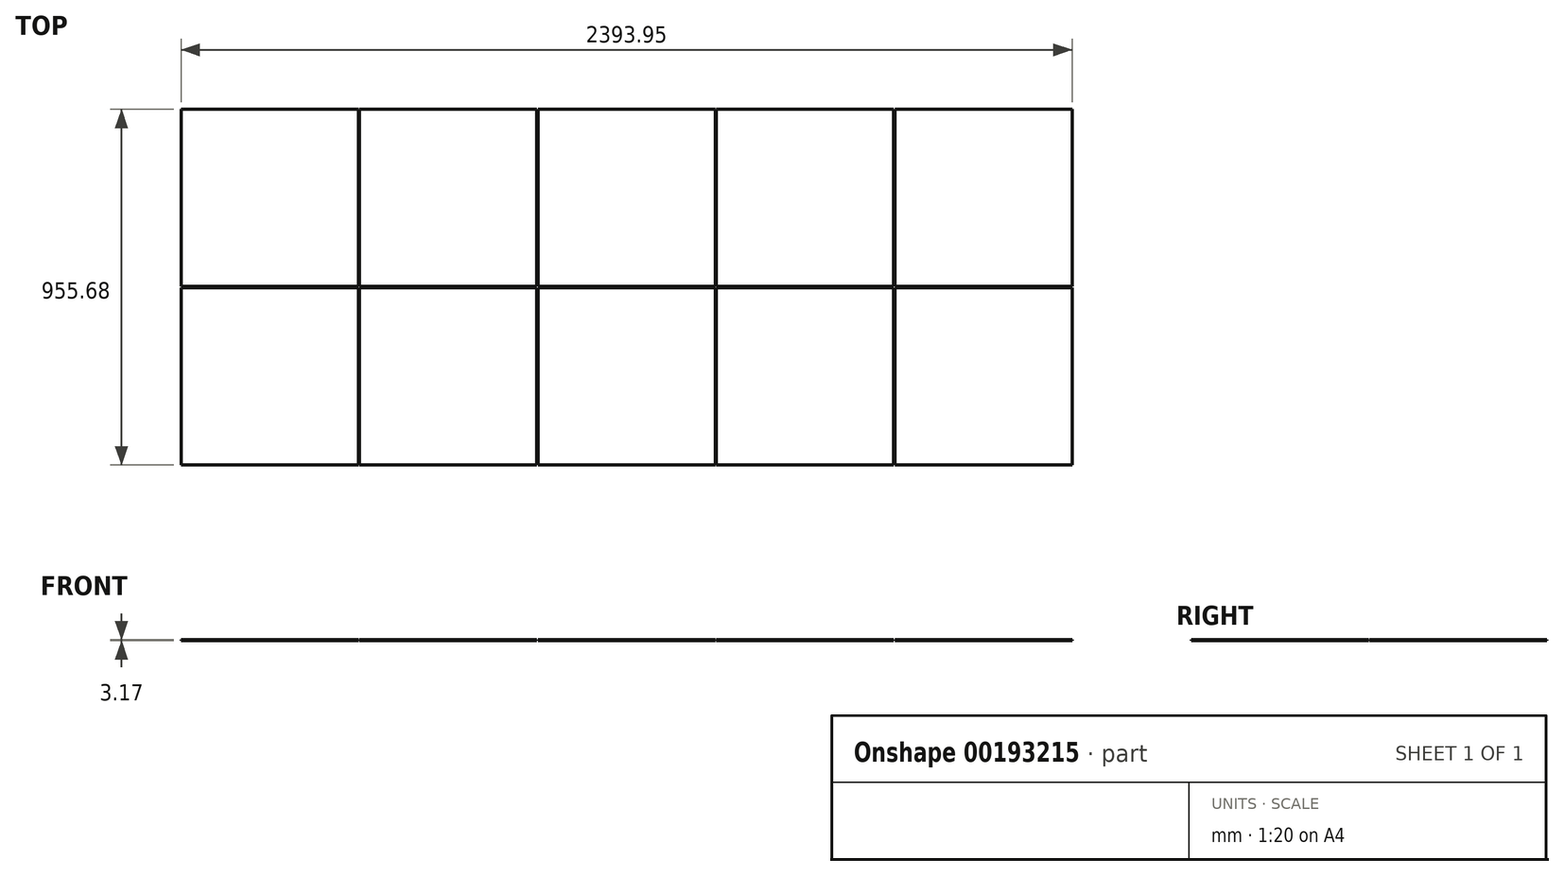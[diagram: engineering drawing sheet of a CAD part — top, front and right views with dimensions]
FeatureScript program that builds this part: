
annotation { "Feature Type Name" : "Feature", "Feature Type Description" : "" }
export const myFeature = defineFeature(function(context is Context, id is Id, definition is map)
    precondition{}
    {
        {
            var Q0;
            Q0=qCreatedBy(makeId("Top.planeOp"),FACE);
            var sketch = newSketch(context, id + "F0", { "sketchPlane" : qUnion([Q0])});
            skLineSegment(sketch, "E0.bottom", {"start": v(0, 0) * mm, "end": v(476.25, 0) * mm});
            skLineSegment(sketch, "E0.top", {"start": v(0, -476.25) * mm, "end": v(476.25, -476.25) * mm});
            skLineSegment(sketch, "E0.left", {"start": v(0, 0) * mm, "end": v(0, -476.25) * mm});
            skLineSegment(sketch, "E0.right", {"start": v(476.25, 0) * mm, "end": v(476.25, -476.25) * mm});
            skLineSegment(sketch, "E1.0.1.0", {"start": v(476.25, 479.43) * mm, "end": v(476.25, 3.18) * mm});
            skLineSegment(sketch, "E1.0.1.1", {"start": v(0, 3.18) * mm, "end": v(476.25, 3.18) * mm});
            skLineSegment(sketch, "E1.0.1.2", {"start": v(0, 479.43) * mm, "end": v(0, 3.18) * mm});
            skLineSegment(sketch, "E1.0.1.3", {"start": v(0, 479.43) * mm, "end": v(476.25, 479.43) * mm});
            skLineSegment(sketch, "E1.1.0.0", {"start": v(955.68, 0) * mm, "end": v(955.68, -476.25) * mm});
            skLineSegment(sketch, "E1.1.0.1", {"start": v(479.43, -476.25) * mm, "end": v(955.68, -476.25) * mm});
            skLineSegment(sketch, "E1.1.0.2", {"start": v(479.43, 0) * mm, "end": v(479.43, -476.25) * mm});
            skLineSegment(sketch, "E1.1.0.3", {"start": v(479.43, 0) * mm, "end": v(955.68, 0) * mm});
            skLineSegment(sketch, "E1.1.1.0", {"start": v(955.68, 479.43) * mm, "end": v(955.68, 3.18) * mm});
            skLineSegment(sketch, "E1.1.1.1", {"start": v(479.43, 3.18) * mm, "end": v(955.68, 3.18) * mm});
            skLineSegment(sketch, "E1.1.1.2", {"start": v(479.43, 479.43) * mm, "end": v(479.43, 3.18) * mm});
            skLineSegment(sketch, "E1.1.1.3", {"start": v(479.43, 479.43) * mm, "end": v(955.68, 479.43) * mm});
            skLineSegment(sketch, "E1.2.0.0", {"start": v(1435.1, 0) * mm, "end": v(1435.1, -476.25) * mm});
            skLineSegment(sketch, "E1.2.0.1", {"start": v(958.85, -476.25) * mm, "end": v(1435.1, -476.25) * mm});
            skLineSegment(sketch, "E1.2.0.2", {"start": v(958.85, 0) * mm, "end": v(958.85, -476.25) * mm});
            skLineSegment(sketch, "E1.2.0.3", {"start": v(958.85, 0) * mm, "end": v(1435.1, 0) * mm});
            skLineSegment(sketch, "E1.2.1.0", {"start": v(1435.1, 479.43) * mm, "end": v(1435.1, 3.18) * mm});
            skLineSegment(sketch, "E1.2.1.1", {"start": v(958.85, 3.18) * mm, "end": v(1435.1, 3.18) * mm});
            skLineSegment(sketch, "E1.2.1.2", {"start": v(958.85, 479.43) * mm, "end": v(958.85, 3.18) * mm});
            skLineSegment(sketch, "E1.2.1.3", {"start": v(958.85, 479.43) * mm, "end": v(1435.1, 479.43) * mm});
            skLineSegment(sketch, "E1.3.0.0", {"start": v(1914.53, 0) * mm, "end": v(1914.53, -476.25) * mm});
            skLineSegment(sketch, "E1.3.0.1", {"start": v(1438.28, -476.25) * mm, "end": v(1914.53, -476.25) * mm});
            skLineSegment(sketch, "E1.3.0.2", {"start": v(1438.27, 0) * mm, "end": v(1438.27, -476.25) * mm});
            skLineSegment(sketch, "E1.3.0.3", {"start": v(1438.27, 0) * mm, "end": v(1914.53, 0) * mm});
            skLineSegment(sketch, "E1.3.1.0", {"start": v(1914.53, 479.43) * mm, "end": v(1914.53, 3.18) * mm});
            skLineSegment(sketch, "E1.3.1.1", {"start": v(1438.28, 3.18) * mm, "end": v(1914.53, 3.18) * mm});
            skLineSegment(sketch, "E1.3.1.2", {"start": v(1438.27, 479.43) * mm, "end": v(1438.27, 3.18) * mm});
            skLineSegment(sketch, "E1.3.1.3", {"start": v(1438.27, 479.43) * mm, "end": v(1914.53, 479.43) * mm});
            skLineSegment(sketch, "E1.4.0.0", {"start": v(2393.95, 0) * mm, "end": v(2393.95, -476.25) * mm});
            skLineSegment(sketch, "E1.4.0.1", {"start": v(1917.7, -476.25) * mm, "end": v(2393.95, -476.25) * mm});
            skLineSegment(sketch, "E1.4.0.2", {"start": v(1917.7, 0) * mm, "end": v(1917.7, -476.25) * mm});
            skLineSegment(sketch, "E1.4.0.3", {"start": v(1917.7, 0) * mm, "end": v(2393.95, 0) * mm});
            skLineSegment(sketch, "E1.4.1.0", {"start": v(2393.95, 479.43) * mm, "end": v(2393.95, 3.18) * mm});
            skLineSegment(sketch, "E1.4.1.1", {"start": v(1917.7, 3.18) * mm, "end": v(2393.95, 3.18) * mm});
            skLineSegment(sketch, "E1.4.1.2", {"start": v(1917.7, 479.43) * mm, "end": v(1917.7, 3.18) * mm});
            skLineSegment(sketch, "E1.4.1.3", {"start": v(1917.7, 479.43) * mm, "end": v(2393.95, 479.43) * mm});
            skLineSegment(sketch, "E1.direction1", {"start": v(476.25, -476.25) * mm, "end": v(955.68, -476.25) * mm, "construction": true});
            skLineSegment(sketch, "E1.direction2", {"start": v(476.25, -476.25) * mm, "end": v(476.25, 3.18) * mm, "construction": true});
            skSolve(sketch);
        }
        {
            var Q0;
            Q0 = qSketchRegion(id + "F0", true);
            extrude(context, id + "F1", {"entities" : qUnion([Q0]), "depth" : 3.17 * mm});
        }
    });
